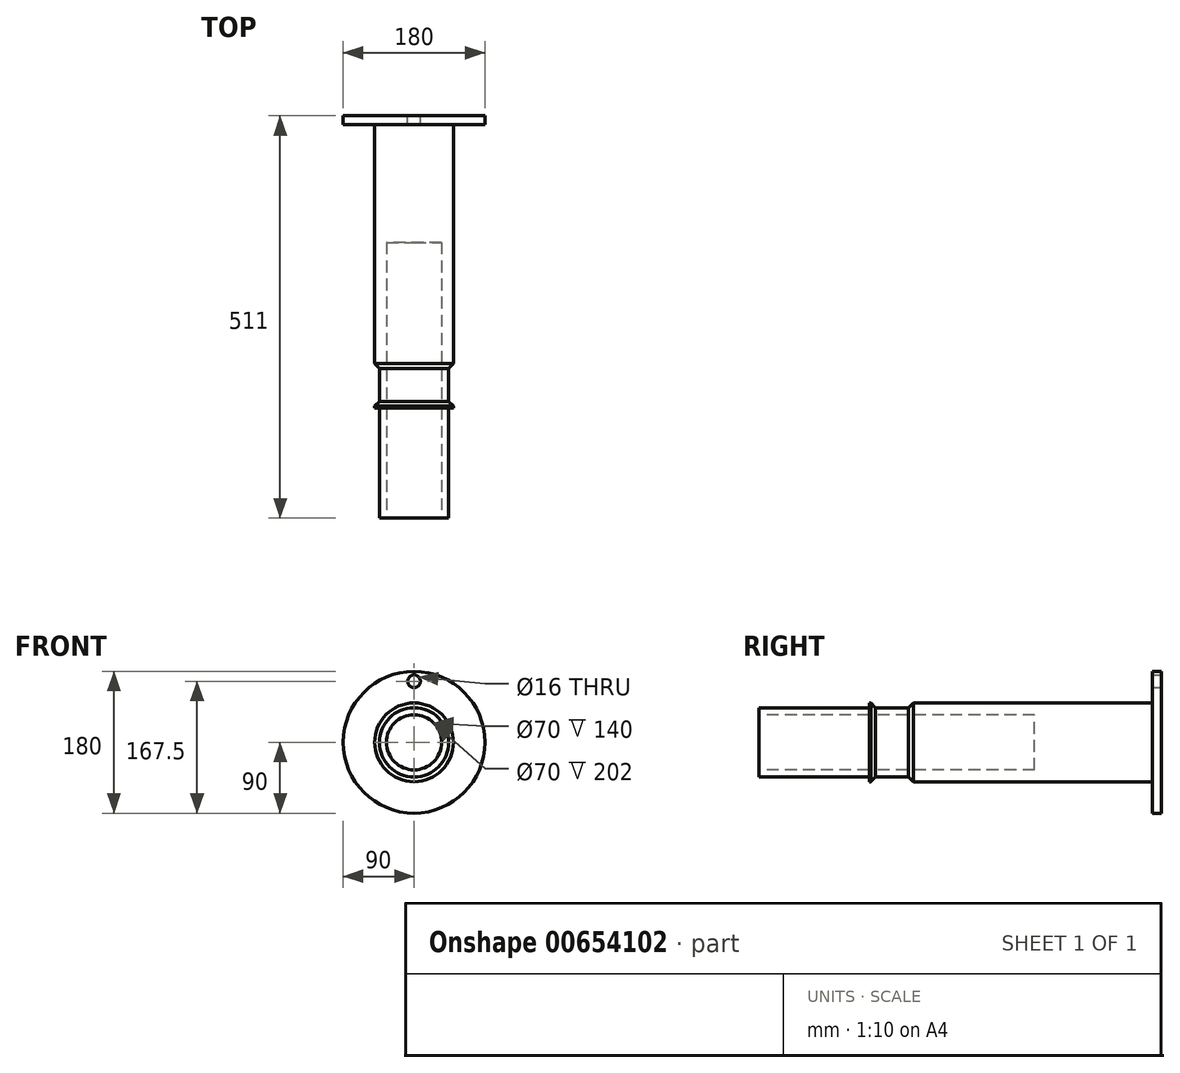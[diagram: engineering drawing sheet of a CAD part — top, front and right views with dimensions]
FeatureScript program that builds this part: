
annotation { "Feature Type Name" : "Feature", "Feature Type Description" : "" }
export const myFeature = defineFeature(function(context is Context, id is Id, definition is map)
    precondition{}
    {
        {
            var Q0;
            Q0=qCreatedBy(makeId("Front.planeOp"),FACE);
            var sketch = newSketch(context, id + "F0", { "sketchPlane" : qUnion([Q0])});
            skCircle(sketch, "E0", {"center": v(0, 0) * mm, "radius": 90 * mm});
            skCircle(sketch, "E1", {"center": v(0, 0) * mm, "radius": 77.5 * mm, "construction": true});
            skCircle(sketch, "E2", {"center": v(0, 77.5) * mm, "radius": 8 * mm});
            skSolve(sketch);
        }
        {
            var Q0;
            Q0 = qSketchRegion(id + "F0", true);
            extrude(context, id + "F1", {"entities" : qUnion([Q0]), "depth" : 11 * mm, "offsetDistance" : 25 * mm});
        }
        {
            var Q0;
            Q0=makeQuery(id+"F1.opExtrude","CAP_FACE",FACE,{"disambiguationData":[OSD([sQuery(id+"F0.wireOp",EDGE,"E0")])],"isStart":false});
            var sketch = newSketch(context, id + "F2", { "sketchPlane" : qUnion([Q0])});
            skCircle(sketch, "E3", {"center": v(0, 0) * mm, "radius": 50 * mm});
            skSolve(sketch);
        }
        {
            var Q0;
            Q0 = qSketchRegion(id + "F2", true);
            extrude(context, id + "F3", {"entities" : qUnion([Q0]), "operationType" : NewBodyOperationType.ADD, "depth" : 310 * mm, "offsetDistance" : 25 * mm});
        }
        {
            var Q0;
            Q0=makeQuery(id+"F3.opExtrude","CAP_FACE",FACE,{"disambiguationData":[OSD([sQuery(id+"F2.wireOp",EDGE,"E3")])],"isStart":false});
            var sketch = newSketch(context, id + "F4", { "sketchPlane" : qUnion([Q0])});
            skCircle(sketch, "E4", {"center": v(0, 0) * mm, "radius": 44 * mm});
            skSolve(sketch);
        }
        {
            var Q0;
            Q0 = qSketchRegion(id + "F4", true);
            extrude(context, id + "F5", {"entities" : qUnion([Q0]), "operationType" : NewBodyOperationType.ADD, "depth" : 190 * mm, "offsetDistance" : 25 * mm});
        }
        {
            var Q0;
            Q0=makeQuery(id+"F5.opExtrude","CAP_FACE",FACE,{"disambiguationData":[OSD([sQuery(id+"F4.wireOp",EDGE,"E4")])],"isStart":false});
            var sketch = newSketch(context, id + "F6", { "sketchPlane" : qUnion([Q0])});
            skCircle(sketch, "E5", {"center": v(0, 0) * mm, "radius": 35 * mm});
            skCircle(sketch, "E6", {"center": v(0, 0) * mm, "radius": 37.5 * mm, "construction": true});
            skSolve(sketch);
        }
        {
            var Q0;
            Q0=makeQuery(id+"F6.imprint","IMPRINT",FACE,{"disambiguationData":[TD([[makeQuery(id+"F6.imprint","IMPRINT",EDGE,{"derivedFrom":sQuery(id+"F6.wireOp",EDGE,"E5")}),1.0]])]});
            extrude(context, id + "F7", {"entities" : qUnion([Q0]), "operationType" : NewBodyOperationType.REMOVE, "oppositeDirection" : true, "depth" : 350 * mm, "offsetDistance" : 25 * mm});
        }
        {
            var Q0;
            Q0=makeQuery(id+"F3.opExtrude","CAP_EDGE",EDGE,{"disambiguationData":[OSD([sQuery(id+"F2.wireOp",EDGE,"E3")])],"isStart":false});
            chamfer(context, id + "F8", {"entities" : qUnion([Q0]), "width" : 6 * mm, "tangentPropagation" : true});
        }
        {
            var Q0;
            Q0=makeQuery(id+"F5.opExtrude","CAP_FACE",FACE,{"disambiguationData":[OSD([sQuery(id+"F4.wireOp",EDGE,"E4")])],"isStart":false});
            cPlane(context, id + "F9", {"entities" : qUnion([Q0]), "cplaneType" : CPlaneType.OFFSET, "offset" : 140 * mm, "oppositeDirection" : true, "width" : 150 * mm, "height" : 150 * mm});
        }
        {
            var Q0;
            Q0=qCreatedBy(id+"F9.planeOp",FACE);
            var sketch = newSketch(context, id + "F10", { "sketchPlane" : qUnion([Q0])});
            skCircle(sketch, "E7", {"center": v(0, 0) * mm, "radius": 50 * mm});
            skSolve(sketch);
        }
        {
            var Q0;
            Q0 = qSketchRegion(id + "F10", true);
            extrude(context, id + "F11", {"entities" : qUnion([Q0]), "operationType" : NewBodyOperationType.ADD, "oppositeDirection" : true, "depth" : 8 * mm, "offsetDistance" : 25 * mm});
        }
        {
            var Q0;
            Q0=makeQuery(id+"F11.opExtrude","CAP_EDGE",EDGE,{"disambiguationData":[OSD([sQuery(id+"F10.wireOp",EDGE,"E7")])],"isStart":false});
            chamfer(context, id + "F12", {"entities" : qUnion([Q0]), "width" : 6 * mm, "tangentPropagation" : true});
        }
    });
